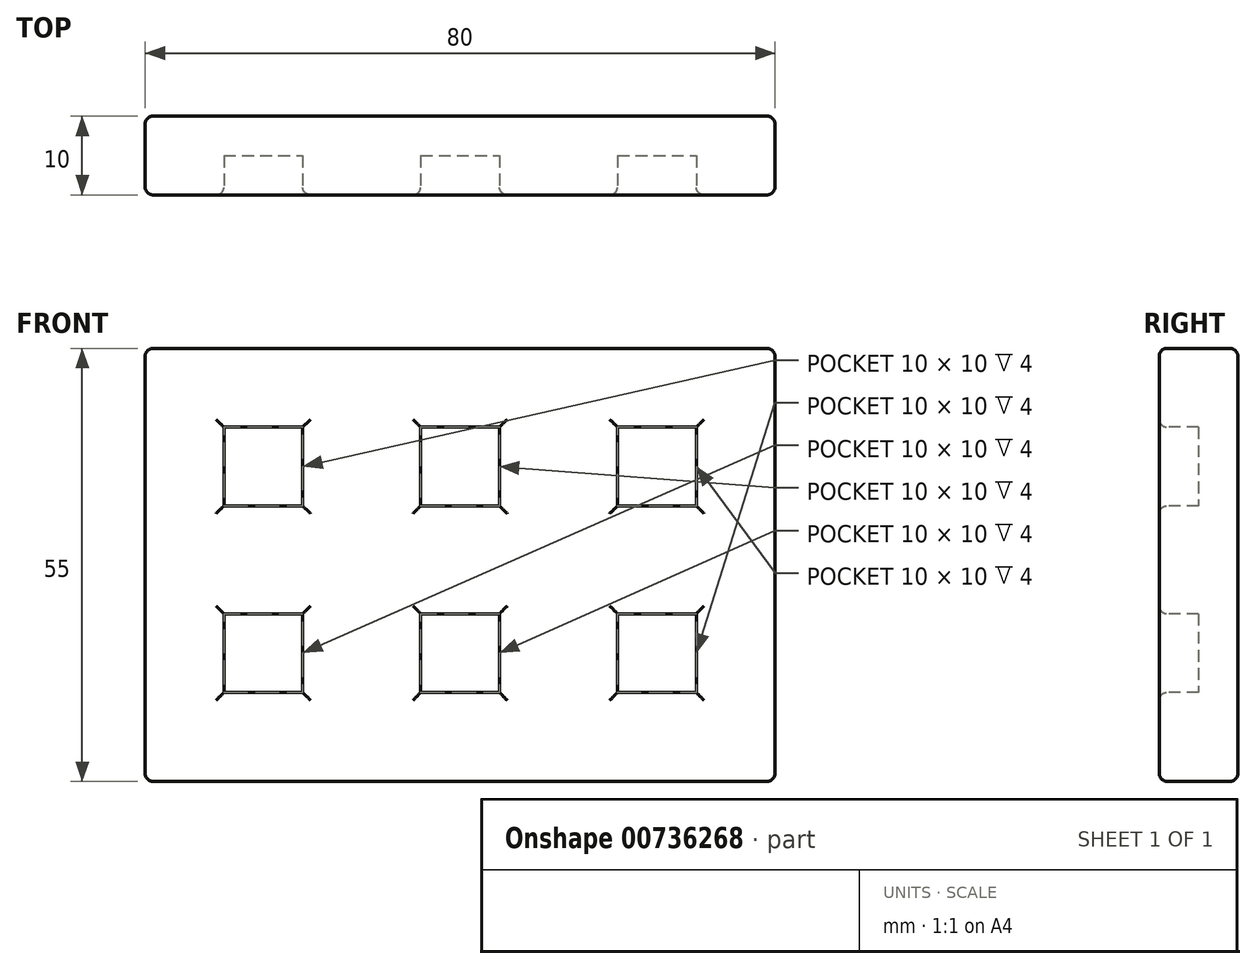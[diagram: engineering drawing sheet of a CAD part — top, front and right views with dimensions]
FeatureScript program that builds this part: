
annotation { "Feature Type Name" : "Feature", "Feature Type Description" : "" }
export const myFeature = defineFeature(function(context is Context, id is Id, definition is map)
    precondition{}
    {
        {
            var Q0;
            Q0=qCreatedBy(makeId("Front.planeOp"),FACE);
            var sketch = newSketch(context, id + "F0", { "sketchPlane" : qUnion([Q0])});
            skLineSegment(sketch, "E0.bottom", {"start": v(-109.61, 34.15) * mm, "end": v(-29.61, 34.15) * mm});
            skLineSegment(sketch, "E0.top", {"start": v(-109.61, -20.85) * mm, "end": v(-29.61, -20.85) * mm});
            skLineSegment(sketch, "E0.left", {"start": v(-109.61, 34.15) * mm, "end": v(-109.61, -20.85) * mm});
            skLineSegment(sketch, "E0.right", {"start": v(-29.61, 34.15) * mm, "end": v(-29.61, -20.85) * mm});
            skSolve(sketch);
        }
        {
            var Q0;
            Q0 = qSketchRegion(id + "F0", true);
            extrude(context, id + "F1", {"entities" : qUnion([Q0]), "depth" : 10 * mm, "offsetDistance" : 25 * mm});
        }
        {
            var Q0;
            Q0=makeQuery(id+"F1.opExtrude","CAP_FACE",FACE,{"disambiguationData":[OSD([sQuery(id+"F0.wireOp",EDGE,"E0.bottom"),sQuery(id+"F0.wireOp",EDGE,"E0.top"),sQuery(id+"F0.wireOp",EDGE,"E0.left"),sQuery(id+"F0.wireOp",EDGE,"E0.right")])],"isStart":false});
            var sketch = newSketch(context, id + "F2", { "sketchPlane" : qUnion([Q0])});
            skLineSegment(sketch, "E1.0", {"start": v(-109.61, 34.15) * mm, "end": v(-29.61, 34.15) * mm, "construction": true});
            skLineSegment(sketch, "E1.1", {"start": v(-29.61, 34.15) * mm, "end": v(-29.61, -20.85) * mm, "construction": true});
            skLineSegment(sketch, "E1.2", {"start": v(-109.61, -20.85) * mm, "end": v(-29.61, -20.85) * mm, "construction": true});
            skLineSegment(sketch, "E1.3", {"start": v(-109.61, 34.15) * mm, "end": v(-109.61, -20.85) * mm, "construction": true});
            skLineSegment(sketch, "E2.bottom", {"start": v(-99.61, 24.15) * mm, "end": v(-89.61, 24.15) * mm});
            skLineSegment(sketch, "E2.top", {"start": v(-99.61, 14.15) * mm, "end": v(-89.61, 14.15) * mm});
            skLineSegment(sketch, "E2.left", {"start": v(-99.61, 24.15) * mm, "end": v(-99.61, 14.15) * mm});
            skLineSegment(sketch, "E2.right", {"start": v(-89.61, 24.15) * mm, "end": v(-89.61, 14.15) * mm});
            skLineSegment(sketch, "E3.0.1.0", {"start": v(-89.61, 0.45) * mm, "end": v(-89.61, -9.55) * mm});
            skLineSegment(sketch, "E3.0.1.1", {"start": v(-99.61, 0.45) * mm, "end": v(-89.61, 0.45) * mm});
            skLineSegment(sketch, "E3.0.1.2", {"start": v(-99.61, -9.55) * mm, "end": v(-89.61, -9.55) * mm});
            skLineSegment(sketch, "E3.0.1.3", {"start": v(-99.61, 0.45) * mm, "end": v(-99.61, -9.55) * mm});
            skLineSegment(sketch, "E3.1.0.0", {"start": v(-64.61, 24.15) * mm, "end": v(-64.61, 14.15) * mm});
            skLineSegment(sketch, "E3.1.0.1", {"start": v(-74.61, 24.15) * mm, "end": v(-64.61, 24.15) * mm});
            skLineSegment(sketch, "E3.1.0.2", {"start": v(-74.61, 14.15) * mm, "end": v(-64.61, 14.15) * mm});
            skLineSegment(sketch, "E3.1.0.3", {"start": v(-74.61, 24.15) * mm, "end": v(-74.61, 14.15) * mm});
            skLineSegment(sketch, "E3.1.1.0", {"start": v(-64.61, 0.45) * mm, "end": v(-64.61, -9.55) * mm});
            skLineSegment(sketch, "E3.1.1.1", {"start": v(-74.61, 0.45) * mm, "end": v(-64.61, 0.45) * mm});
            skLineSegment(sketch, "E3.1.1.2", {"start": v(-74.61, -9.55) * mm, "end": v(-64.61, -9.55) * mm});
            skLineSegment(sketch, "E3.1.1.3", {"start": v(-74.61, 0.45) * mm, "end": v(-74.61, -9.55) * mm});
            skLineSegment(sketch, "E3.2.0.0", {"start": v(-39.61, 24.15) * mm, "end": v(-39.61, 14.15) * mm});
            skLineSegment(sketch, "E3.2.0.1", {"start": v(-49.61, 24.15) * mm, "end": v(-39.61, 24.15) * mm});
            skLineSegment(sketch, "E3.2.0.2", {"start": v(-49.61, 14.15) * mm, "end": v(-39.61, 14.15) * mm});
            skLineSegment(sketch, "E3.2.0.3", {"start": v(-49.61, 24.15) * mm, "end": v(-49.61, 14.15) * mm});
            skLineSegment(sketch, "E3.2.1.0", {"start": v(-39.61, 0.45) * mm, "end": v(-39.61, -9.55) * mm});
            skLineSegment(sketch, "E3.2.1.1", {"start": v(-49.61, 0.45) * mm, "end": v(-39.61, 0.45) * mm});
            skLineSegment(sketch, "E3.2.1.2", {"start": v(-49.61, -9.55) * mm, "end": v(-39.61, -9.55) * mm});
            skLineSegment(sketch, "E3.2.1.3", {"start": v(-49.61, 0.45) * mm, "end": v(-49.61, -9.55) * mm});
            skLineSegment(sketch, "E3.direction1", {"start": v(-99.61, 14.15) * mm, "end": v(-74.61, 14.15) * mm, "construction": true});
            skLineSegment(sketch, "E3.direction2", {"start": v(-99.61, 14.15) * mm, "end": v(-99.61, -9.55) * mm, "construction": true});
            skSolve(sketch);
        }
        {
            var Q0;
            Q0 = qSketchRegion(id + "F2", true);
            extrude(context, id + "F3", {"entities" : qUnion([Q0]), "operationType" : NewBodyOperationType.REMOVE, "oppositeDirection" : true, "depth" : 5 * mm, "offsetDistance" : 25 * mm});
        }
        {
            var Q0;
            Q0=makeQuery(id+"F1.opExtrude","CAP_FACE",FACE,{"disambiguationData":[OSD([sQuery(id+"F0.wireOp",EDGE,"E0.bottom"),sQuery(id+"F0.wireOp",EDGE,"E0.top"),sQuery(id+"F0.wireOp",EDGE,"E0.left"),sQuery(id+"F0.wireOp",EDGE,"E0.right")])],"isStart":false});
            var Q1;
            Q1=makeQuery(id+"F1.opExtrude","CAP_FACE",FACE,{"disambiguationData":[OSD([sQuery(id+"F0.wireOp",EDGE,"E0.bottom"),sQuery(id+"F0.wireOp",EDGE,"E0.top"),sQuery(id+"F0.wireOp",EDGE,"E0.left"),sQuery(id+"F0.wireOp",EDGE,"E0.right")])],"isStart":true});
            var Q2;
            Q2=makeQuery(id+"F1.opExtrude","SWEPT_EDGE",EDGE,{"disambiguationData":[OSD([sQuery(id+"F0.wireOp",EDGE,"E0.bottom"),sQuery(id+"F0.wireOp",EDGE,"E0.right")])]});
            var Q3;
            Q3=makeQuery(id+"F1.opExtrude","SWEPT_EDGE",EDGE,{"disambiguationData":[OSD([sQuery(id+"F0.wireOp",EDGE,"E0.top"),sQuery(id+"F0.wireOp",EDGE,"E0.right")])]});
            var Q4;
            Q4=makeQuery(id+"F1.opExtrude","SWEPT_FACE",FACE,{"disambiguationData":[OSD([sQuery(id+"F0.wireOp",EDGE,"E0.left")])]});
            fillet(context, id + "F4", {"entities" : qUnion([Q0, Q1, Q2, Q3, Q4]), "radius" : 1 * mm, "tangentPropagation" : true, "allowEdgeOverflow" : false});
        }
    });
